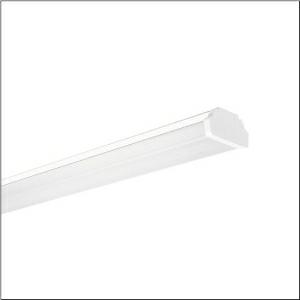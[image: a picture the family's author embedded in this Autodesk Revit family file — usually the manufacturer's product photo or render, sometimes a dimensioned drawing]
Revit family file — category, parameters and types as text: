
# Revit family: dus_r__31_gen_2_53bd812dv4a5c23sl3_a75a
name_source: partatom
category: Lighting Fixtures
units: mm (PartAtom-declared; Revit-internal decimal feet)

## family parameters
Cut with Voids When Loaded = No
Host = Face
Light Source = No
Part Type = Normal
Room Calculation Point = No
Round Connector Dimension = Use Diameter
Shared = No

## types (1)
- --- (1 x LED, 950 lm, 6.3 W, 4000K)
    Apparent Load = 6 VA
    CIE Flux Codes = 47 80 95 93 100
    Color Rendering = 80
    Color Temperature = 4000K
    Default Elevation = 1800 mm
    Description = DUS® 31 Gen.2, luminaire insert, of sheet steel, coil coated, white, length: 1.535mm, width: 81mm, height: 90mm, 5x system unit, system units: 307mm, LED rated luminous flux: 10.860lm, light colour: 840, control gear: DALI 2, with plug, 6-pole, with phase selection (L1, L2), mains connection: 220..240V, AC, 50/60Hz, rated input power: 65W, for emergency light function, charging phase on L3 (wire number 3), through-wiring accessed according to module size, converter,control gear: single battery element, battery: LiFePO4, 9Ah, primary optical cover: cover, of PMMA, light emission: direct distribution, primary light characteristic: symmetric, protection rating (complete): IP20, protection rating (LED compartment): IP50, insulation class (complete): insulation class I (protective earthing), certification: CE, UKCA, impact resistance: IK03, permissible ambient temperature for indoor applications: +5..+35°C, standard: EN 60598-2-22, corresponds to IFS (International Featured Standards) requirements for safety and quality in the food industry, reducing of maximum allowable ambient temperature of 5°C with ceiling mounting, packaging unit: 1 piece
    Height = 95 mm
    Lamp = 1 x LED
    Lamp Light Flux = 950 lm
    Lamp Power = 6.3 W
    Lamp count = 1
    Length = 1535 mm
    Luminous efficacy = 151 lm/W
    Manufacturer = Siteco
    ModVariant = No
    Model = 53BD812DV4A5C23SL3
    Mounting Place = Ceiling
    Mounting Type = Pendant
    Number of Poles = 1
    OnlyDefault = Yes
    Power Factor = 1
    Product Name = DUS® 31 Gen.2
    Product group = luminaire insert
    ProductGroupID = 902
    Protection Class = Protection class I
    Protection Degree = IP 20
    RLX_Detail_Level = 1
    RLX_Emergency_Light_Flux = 0 lm
    RLX_Emergency_Type = 0
    RLX_Emergency_Type_DB = No
    RlxData = <blob elided: 32305 chars, md5=317613d7>
    Socket = socket
    Standby Power = 0 W
    System Light Flux = 950 lm
    System Power = 6 W
    Type Comments = : emergency light operation: 3 h
    Type Image = l_1319596.jpg
    URL = http://relux.com
    VarID = @adj_022234
    Voltage = 0 V
    Weight = 0.00 kg
    Width = 81 mm

## geometry (parser evidence)
native form markers: Blend x4, Sweep x12
no freeform markers — native parametric forms only
